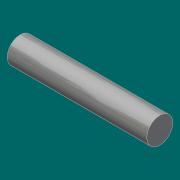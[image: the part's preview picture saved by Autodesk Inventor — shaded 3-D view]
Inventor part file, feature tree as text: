
AUTODESK INVENTOR PART (.ipt)
format: ipt  version: 2017.3 (Build 213257000, 257)  size: 129,024 bytes
history: native  units: in
note: dims shown in document units (in); Inventor stores cm internally (conversion verified against a paired STEP export)
features: revolve x1, sketch x1
ambient origin geometry x8: Origin, YZ Plane, XZ Plane, XY Plane, X Axis, Y Axis, Z Axis, Center Point
bodies: Solid1 (feature_tree)
feature tree (2):
  revolve  "Revolution1"  [1 undecoded]
  sketch  "Sketch1"  dims[d0=5.375in d1=1.0in d5=90.0deg]
note: 1 required parameter value undecoded (feature->parameter linkage not recoverable at this tier; creation-order binding heuristic only, values carry confidence <= 0.55)
